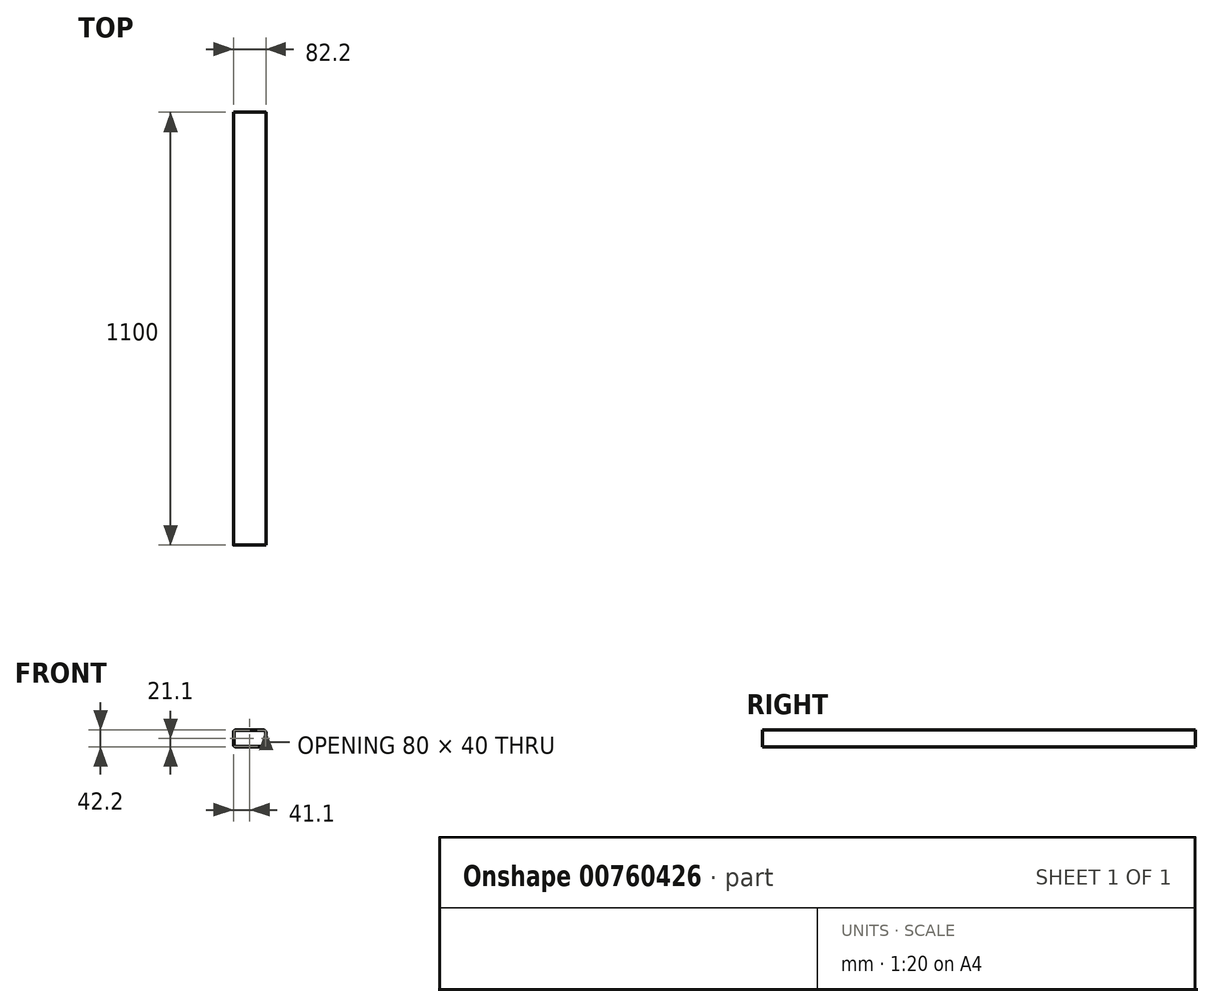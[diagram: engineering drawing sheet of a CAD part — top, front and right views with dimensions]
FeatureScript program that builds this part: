
annotation { "Feature Type Name" : "Feature", "Feature Type Description" : "" }
export const myFeature = defineFeature(function(context is Context, id is Id, definition is map)
    precondition{}
    {
        {
            assignVariable(context, id + "F0", {"name" : "LENGTH", "anyValue" : 1100});
        }
        {
            var Q0;
            Q0=qCreatedBy(makeId("Front.planeOp"),FACE);
            var sketch = newSketch(context, id + "F1", { "sketchPlane" : qUnion([Q0])});
            skLineSegment(sketch, "E0.bottom", {"start": v(-35, 20) * mm, "end": v(35, 20) * mm});
            skLineSegment(sketch, "E0.top", {"start": v(-35, -20) * mm, "end": v(35, -20) * mm});
            skLineSegment(sketch, "E0.left", {"start": v(-40, 15) * mm, "end": v(-40, -15) * mm});
            skLineSegment(sketch, "E0.right", {"start": v(40, 15) * mm, "end": v(40, -15) * mm});
            skPoint(sketch, "E1.visualSharp", {"position": v(-40, 20) * mm});
            skArc(sketch, "E1.filletArc", {"start": v(-35, 20) * mm, "mid": v(-38.54, 18.54) * mm, "end": v(-40, 15) * mm});
            skPoint(sketch, "E2.visualSharp", {"position": v(40, 20) * mm});
            skArc(sketch, "E2.filletArc", {"start": v(40, 15) * mm, "mid": v(38.54, 18.54) * mm, "end": v(35, 20) * mm});
            skPoint(sketch, "E3.visualSharp", {"position": v(40, -20) * mm});
            skArc(sketch, "E3.filletArc", {"start": v(35, -20) * mm, "mid": v(38.54, -18.54) * mm, "end": v(40, -15) * mm});
            skPoint(sketch, "E4.visualSharp", {"position": v(-40, -20) * mm});
            skArc(sketch, "E4.filletArc", {"start": v(-40, -15) * mm, "mid": v(-38.54, -18.54) * mm, "end": v(-35, -20) * mm});
            skLineSegment(sketch, "E5.0", {"start": v(41.1, 16.1) * mm, "end": v(41.1, -16.1) * mm});
            skLineSegment(sketch, "E5.1", {"start": v(-36.1, 21.1) * mm, "end": v(36.1, 21.1) * mm});
            skLineSegment(sketch, "E5.2", {"start": v(-41.1, 16.1) * mm, "end": v(-41.1, -16.1) * mm});
            skLineSegment(sketch, "E5.3", {"start": v(-36.1, -21.1) * mm, "end": v(36.1, -21.1) * mm});
            skPoint(sketch, "E6.visualSharp", {"position": v(-41.1, 21.1) * mm});
            skArc(sketch, "E6.filletArc", {"start": v(-36.1, 21.1) * mm, "mid": v(-39.64, 19.64) * mm, "end": v(-41.1, 16.1) * mm});
            skPoint(sketch, "E7.visualSharp", {"position": v(41.1, 21.1) * mm});
            skArc(sketch, "E7.filletArc", {"start": v(41.1, 16.1) * mm, "mid": v(39.64, 19.64) * mm, "end": v(36.1, 21.1) * mm});
            skPoint(sketch, "E8.visualSharp", {"position": v(41.1, -21.1) * mm});
            skArc(sketch, "E8.filletArc", {"start": v(36.1, -21.1) * mm, "mid": v(39.64, -19.64) * mm, "end": v(41.1, -16.1) * mm});
            skPoint(sketch, "E9.visualSharp", {"position": v(-41.1, -21.1) * mm});
            skArc(sketch, "E9.filletArc", {"start": v(-41.1, -16.1) * mm, "mid": v(-39.64, -19.64) * mm, "end": v(-36.1, -21.1) * mm});
            skSolve(sketch);
        }
        {
            var Q0;
            Q0=makeQuery(id+"F1.imprint","IMPRINT",FACE,{"disambiguationData":[TD([[makeQuery(id+"F1.imprint","IMPRINT",EDGE,{"derivedFrom":sQuery(id+"F1.wireOp",EDGE,"E0.bottom")}),1.0]])]});
            extrude(context, id + "F2", {"entities" : qUnion([Q0]), "depth" : (getVariable(context, 'LENGTH')) * mm, "offsetDistance" : 25 * mm});
        }
        {
            var Q0;
            Q0=qCreatedBy(makeId("Front.planeOp"),FACE);
            var sketch = newSketch(context, id + "F3", { "sketchPlane" : qUnion([Q0])});
            skPoint(sketch, "E10", {"position": v(0, 0) * mm});
            skSolve(sketch);
        }
        {
            var Q0;
            Q0=makeQuery(id+"F2.opExtrude","CAP_FACE",FACE,{"disambiguationData":[OSD([sQuery(id+"F1.wireOp",EDGE,"E0.bottom"),sQuery(id+"F1.wireOp",EDGE,"E0.top"),sQuery(id+"F1.wireOp",EDGE,"E0.left"),sQuery(id+"F1.wireOp",EDGE,"E0.right"),sQuery(id+"F1.wireOp",EDGE,"E1.filletArc"),sQuery(id+"F1.wireOp",EDGE,"E2.filletArc"),sQuery(id+"F1.wireOp",EDGE,"E3.filletArc"),sQuery(id+"F1.wireOp",EDGE,"E4.filletArc"),sQuery(id+"F1.wireOp",EDGE,"E5.0"),sQuery(id+"F1.wireOp",EDGE,"E5.1"),sQuery(id+"F1.wireOp",EDGE,"E5.2"),sQuery(id+"F1.wireOp",EDGE,"E5.3"),sQuery(id+"F1.wireOp",EDGE,"E6.filletArc"),sQuery(id+"F1.wireOp",EDGE,"E7.filletArc"),sQuery(id+"F1.wireOp",EDGE,"E8.filletArc"),sQuery(id+"F1.wireOp",EDGE,"E9.filletArc")])],"isStart":false});
            var sketch = newSketch(context, id + "F4", { "sketchPlane" : qUnion([Q0])});
            skPoint(sketch, "E11", {"position": v(0, 0) * mm});
            skSolve(sketch);
        }
    });
